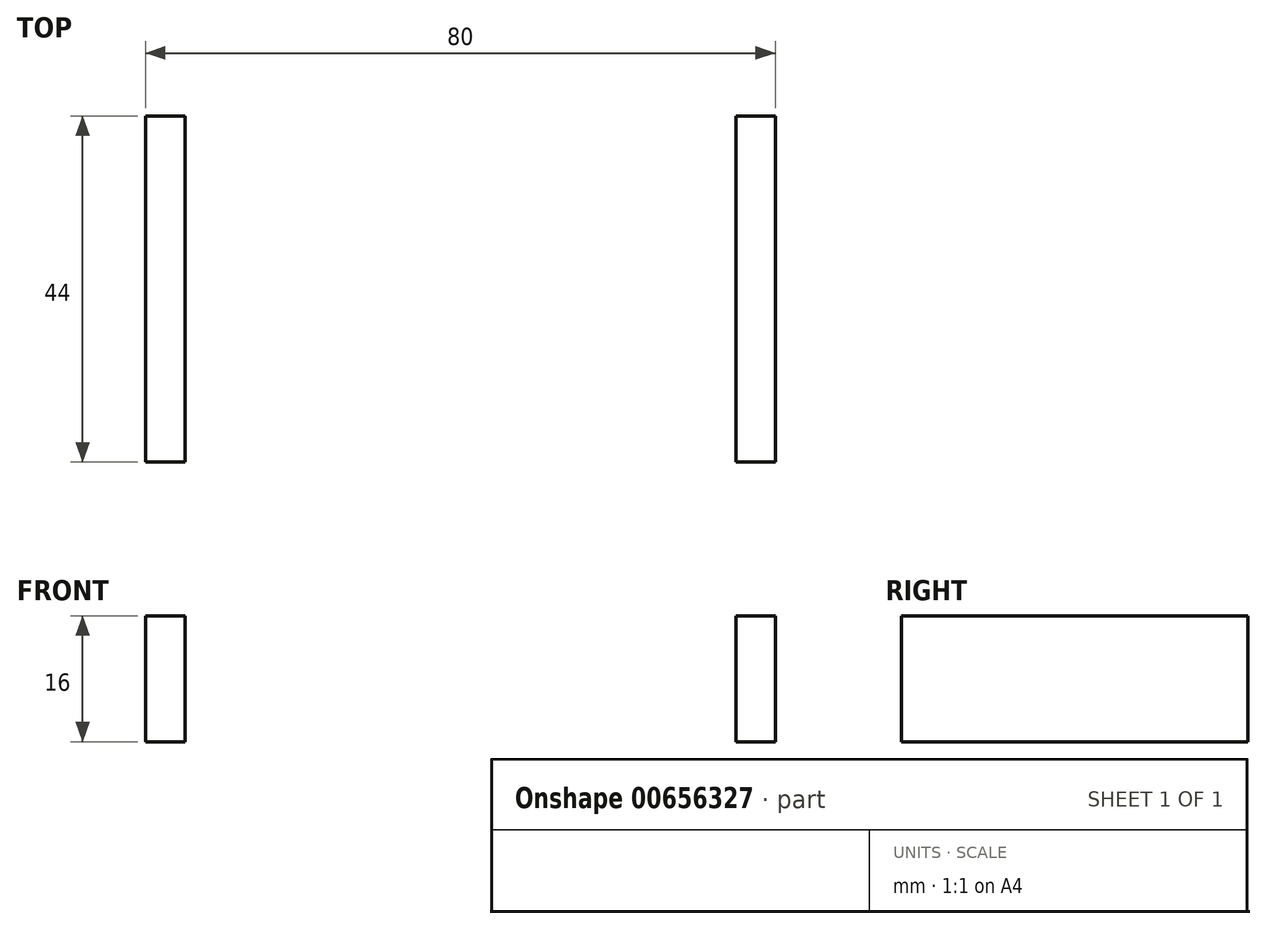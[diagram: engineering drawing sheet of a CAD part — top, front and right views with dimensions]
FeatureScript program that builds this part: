
annotation { "Feature Type Name" : "Feature", "Feature Type Description" : "" }
export const myFeature = defineFeature(function(context is Context, id is Id, definition is map)
    precondition{}
    {
        {
            var Q0;
            Q0=qCreatedBy(makeId("Top.planeOp"),FACE);
            var sketch = newSketch(context, id + "F0", { "sketchPlane" : qUnion([Q0])});
            skLineSegment(sketch, "E0.bottom", {"start": v(40, 22) * mm, "end": v(-40, 22) * mm});
            skLineSegment(sketch, "E0.top", {"start": v(40, -22) * mm, "end": v(-40, -22) * mm});
            skLineSegment(sketch, "E0.left", {"start": v(40, 22) * mm, "end": v(40, -22) * mm});
            skLineSegment(sketch, "E0.right", {"start": v(-40, 22) * mm, "end": v(-40, -22) * mm});
            skPoint(sketch, "E0.middle", {"position": v(0, 0) * mm});
            skLineSegment(sketch, "E1.bottom", {"start": v(25, 22) * mm, "end": v(-25, 22) * mm});
            skLineSegment(sketch, "E1.top", {"start": v(25, -22) * mm, "end": v(-25, -22) * mm});
            skLineSegment(sketch, "E1.left", {"start": v(25, 22) * mm, "end": v(25, -22) * mm});
            skLineSegment(sketch, "E1.right", {"start": v(-25, 22) * mm, "end": v(-25, -22) * mm});
            skLineSegment(sketch, "E2.bottom", {"start": v(25, 22) * mm, "end": v(35, 22) * mm});
            skLineSegment(sketch, "E2.top", {"start": v(25, -22) * mm, "end": v(35, -22) * mm});
            skLineSegment(sketch, "E2.right", {"start": v(35, 22) * mm, "end": v(35, -22) * mm});
            skLineSegment(sketch, "E3.bottom", {"start": v(-25, -22) * mm, "end": v(-35, -22) * mm});
            skLineSegment(sketch, "E3.top", {"start": v(-25, 22) * mm, "end": v(-35, 22) * mm});
            skLineSegment(sketch, "E3.left", {"start": v(-25, -22) * mm, "end": v(-25, 22) * mm});
            skLineSegment(sketch, "E3.right", {"start": v(-35, -22) * mm, "end": v(-35, 22) * mm});
            skLineSegment(sketch, "E4", {"start": v(-25, 0) * mm, "end": v(-35, 0) * mm});
            skLineSegment(sketch, "E5", {"start": v(25, 0) * mm, "end": v(35, 0) * mm});
            skSolve(sketch);
        }
        {
            var Q0;
            {var subQ0=sQuery(id+"F0.wireOp",EDGE,"E0.right");Q0=makeQuery(id+"F0.imprint","IMPRINT",FACE,{"disambiguationData":[TD([[makeQuery(id+"F0.imprint","IMPRINT",EDGE,{"derivedFrom":subQ0}),1.0]])]});}
            var Q1;
            {var subQ0=sQuery(id+"F0.wireOp",EDGE,"E3.top");Q1=makeQuery(id+"F0.imprint","IMPRINT",FACE,{"disambiguationData":[TD([[makeQuery(id+"F0.imprint","IMPRINT",EDGE,{"derivedFrom":subQ0}),1.0]])]});}
            var Q2;
            {var subQ0=sQuery(id+"F0.wireOp",EDGE,"E3.bottom");Q2=makeQuery(id+"F0.imprint","IMPRINT",FACE,{"disambiguationData":[TD([[makeQuery(id+"F0.imprint","IMPRINT",EDGE,{"derivedFrom":subQ0}),-1.0]])]});}
            var Q3;
            {var subQ1=sQuery(id+"F0.wireOp",EDGE,"E1.bottom");Q3=makeQuery(id+"F0.imprint","IMPRINT",FACE,{"disambiguationData":[TD([[makeQuery(id+"F0.imprint","IMPRINT",EDGE,{"derivedFrom":subQ1}),1.0]])]});}
            var Q4;
            {var subQ0=sQuery(id+"F0.wireOp",EDGE,"E2.bottom");Q4=makeQuery(id+"F0.imprint","IMPRINT",FACE,{"disambiguationData":[TD([[makeQuery(id+"F0.imprint","IMPRINT",EDGE,{"derivedFrom":subQ0}),-1.0]])]});}
            var Q5;
            {var subQ0=sQuery(id+"F0.wireOp",EDGE,"E2.top");Q5=makeQuery(id+"F0.imprint","IMPRINT",FACE,{"disambiguationData":[TD([[makeQuery(id+"F0.imprint","IMPRINT",EDGE,{"derivedFrom":subQ0}),1.0]])]});}
            var Q6;
            {var subQ0=sQuery(id+"F0.wireOp",EDGE,"E0.left");Q6=makeQuery(id+"F0.imprint","IMPRINT",FACE,{"disambiguationData":[TD([[makeQuery(id+"F0.imprint","IMPRINT",EDGE,{"derivedFrom":subQ0}),-1.0]])]});}
            extrude(context, id + "F1", {"entities" : qUnion([Q0, Q1, Q2, Q3, Q4, Q5, Q6]), "depth" : 16 * mm, "offsetDistance" : 25 * mm});
        }
        {
            var Q0;
            Q0=makeQuery(id+"F1.opExtrude","CAP_FACE",FACE,{"disambiguationData":[OSD([sQuery(id+"F0.wireOp",EDGE,"E0.bottom"),sQuery(id+"F0.wireOp",EDGE,"E0.top"),sQuery(id+"F0.wireOp",EDGE,"E0.left"),sQuery(id+"F0.wireOp",EDGE,"E0.right"),sQuery(id+"F0.wireOp",EDGE,"E1.bottom"),sQuery(id+"F0.wireOp",EDGE,"E1.top"),sQuery(id+"F0.wireOp",EDGE,"E2.bottom"),sQuery(id+"F0.wireOp",EDGE,"E2.top"),sQuery(id+"F0.wireOp",EDGE,"E3.bottom"),sQuery(id+"F0.wireOp",EDGE,"E3.top")])],"isStart":false});
            var sketch = newSketch(context, id + "F2", { "sketchPlane" : qUnion([Q0])});
            skLineSegment(sketch, "E6.bottom", {"start": v(25, 22) * mm, "end": v(-25, 22) * mm});
            skLineSegment(sketch, "E6.top", {"start": v(25, -22) * mm, "end": v(-25, -22) * mm});
            skLineSegment(sketch, "E6.left", {"start": v(25, 22) * mm, "end": v(25, -22) * mm});
            skLineSegment(sketch, "E6.right", {"start": v(-25, 22) * mm, "end": v(-25, -22) * mm});
            skPoint(sketch, "E6.middle", {"position": v(0, 0) * mm});
            skLineSegment(sketch, "E7.bottom", {"start": v(35, 22) * mm, "end": v(-35, 22) * mm});
            skLineSegment(sketch, "E7.top", {"start": v(35, -22) * mm, "end": v(-35, -22) * mm});
            skLineSegment(sketch, "E7.left", {"start": v(35, 22) * mm, "end": v(35, -22) * mm});
            skLineSegment(sketch, "E7.right", {"start": v(-35, 22) * mm, "end": v(-35, -22) * mm});
            skLineSegment(sketch, "E8", {"start": v(-35, 0) * mm, "end": v(35, 0) * mm});
            skSolve(sketch);
        }
        {
            var Q0;
            {var subQ0=sQuery(id+"F2.wireOp",EDGE,"E7.bottom");var subQ1=sQuery(id+"F2.wireOp",EDGE,"E6.right");var subQ2=makeQuery(id+"F2.imprint","INTERSECT",VERTEX,{"derivedFrom":[subQ1,subQ0]});Q0=makeQuery(id+"F2.imprint","IMPRINT",FACE,{"disambiguationData":[TD([[makeQuery(id+"F2.imprint","IMPRINT",EDGE,{"disambiguationData":[TD([[subQ2,-1.0]])],"derivedFrom":subQ1}),-1.0]])]});}
            var Q1;
            {var subQ0=sQuery(id+"F2.wireOp",EDGE,"E7.top");var subQ1=sQuery(id+"F2.wireOp",EDGE,"E6.left");var subQ2=makeQuery(id+"F2.imprint","INTERSECT",VERTEX,{"derivedFrom":[subQ1,subQ0]});Q1=makeQuery(id+"F2.imprint","IMPRINT",FACE,{"disambiguationData":[TD([[makeQuery(id+"F2.imprint","IMPRINT",EDGE,{"disambiguationData":[TD([[subQ2,1.0]])],"derivedFrom":subQ1}),1.0]])]});}
            extrude(context, id + "F3", {"entities" : qUnion([Q0, Q1]), "operationType" : NewBodyOperationType.REMOVE, "oppositeDirection" : true, "depth" : 8 * mm, "offsetDistance" : 25 * mm});
        }
    });
